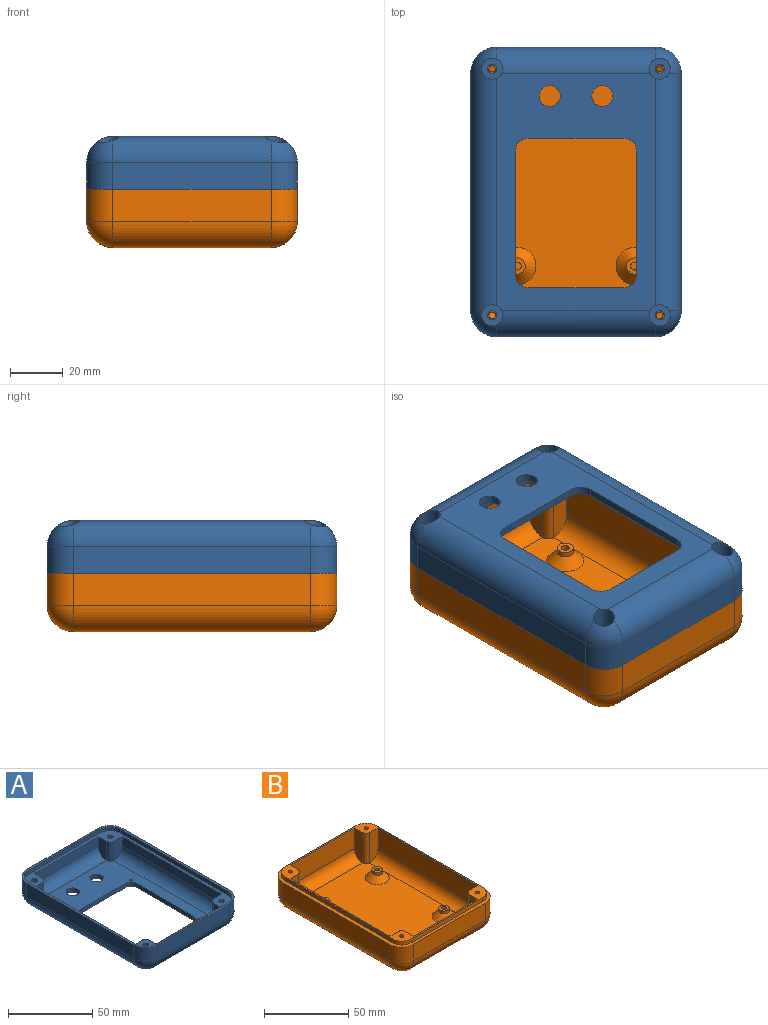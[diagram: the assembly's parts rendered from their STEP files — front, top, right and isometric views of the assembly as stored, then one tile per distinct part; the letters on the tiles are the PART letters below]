
ASSEMBLY  parts=2 mates=1
PART A: 78 faces, bbox 80x110x20 mm
  f0: plane 90x60mm, normal (0,0,-1), area 2700.5mm2, adj f1,f3,f4,f6,f31,f32,f33,f34
  f1: cylinder r=10mm len=90mm, axis (0,1,0), area 1394.3mm2, adj f0,f2,f11,f23,f65,f66
  f2: sphere r=10mm, area 123.8mm2, adj f1,f3,f30,f65
  f3: cylinder r=10mm len=60mm, axis (1,0,0), area 923.1mm2, adj f0,f2,f12,f29,f62,f65
  f4: cylinder r=10mm len=60mm, axis (-1,0,0), area 923.1mm2, adj f0,f5,f11,f25,f66,f69
  f5: sphere r=10mm, area 123.8mm2, adj f4,f6,f26,f69
  f6: cylinder r=10mm len=90mm, axis (0,-1,0), area 1394.3mm2, adj f0,f5,f12,f27,f62,f69
  f7: cylinder r=1.75mm len=3.5mm, axis (0,0,1), area 22mm2, adj f49,f68
  f8: cylinder r=1.75mm len=3.5mm, axis (0,0,1), area 22mm2, adj f49,f67
  f9: cylinder r=1.75mm len=3.5mm, axis (0,0,1), area 22mm2, adj f49,f64
  f10: cylinder r=1.75mm len=3.5mm, axis (0,0,1), area 22mm2, adj f49,f63
  f11: sphere r=10mm, area 123.8mm2, adj f1,f4,f24,f66
  f12: sphere r=10mm, area 123.8mm2, adj f3,f6,f28,f62
  f13: plane 84x7mm, normal (1,0,0), area 588mm2, adj f21,f49,f52,f61
  f14: plane 54x7mm, normal (0,1,0), area 378mm2, adj f18,f49,f56,f60
  f15: plane 84x7mm, normal (-1,0,0), area 588mm2, adj f17,f49,f55,f58
  f16: plane 90x60mm, normal (0,0,1), area 2667.3mm2, adj f17,f18,f20,f21,f31,f32,f33,f34
  f17: cylinder r=7mm len=84mm, axis (0,1,0), area 923.6mm2, adj f15,f16,f55,f58
  f18: cylinder r=7mm len=54mm, axis (1,0,0), area 593.8mm2, adj f14,f16,f56,f60
  f19: plane 54x7mm, normal (0,-1,0), area 378mm2, adj f20,f49,f50,f54
  f20: cylinder r=7mm len=54mm, axis (-1,0,0), area 593.8mm2, adj f16,f19,f50,f54
  f21: cylinder r=7mm len=84mm, axis (0,-1,0), area 923.6mm2, adj f13,f16,f52,f61
  f22: plane 110x80mm, normal (0,0,1), area 484.1mm2, adj f23,f24,f25,f26,f27,f28,f29,f30
  f23: plane 90x10mm, normal (1,0,0), area 900mm2, adj f1,f22,f24,f30
  f24: cylinder r=10mm len=10mm, axis (0,0,-1), area 157.1mm2, adj f11,f22,f23,f25
  f25: plane 60x10mm, normal (0,1,0), area 600mm2, adj f4,f22,f24,f26
  f26: cylinder r=10mm len=10mm, axis (0,0,-1), area 157.1mm2, adj f5,f22,f25,f27
  f27: plane 90x10mm, normal (-1,0,0), area 900mm2, adj f6,f22,f26,f28
  f28: cylinder r=10mm len=10mm, axis (0,0,-1), area 157.1mm2, adj f12,f22,f27,f29
  f29: plane 60x10mm, normal (0,-1,0), area 600mm2, adj f3,f22,f28,f30
  f30: cylinder r=10mm len=10mm, axis (0,0,-1), area 157.1mm2, adj f2,f22,f23,f29
  f31: cylinder r=4mm len=8mm, axis (0,0,1), area 75.4mm2, adj f0,f16
  f32: cylinder r=4mm len=8mm, axis (0,0,1), area 75.4mm2, adj f0,f16
  f33: plane 46.8x3mm, normal (-1,0,0), area 140.4mm2, adj f0,f16,f34,f40
  f34: cylinder r=5mm len=5mm, axis (0,0,1), area 23.6mm2, adj f0,f16,f33,f35
  f35: plane 36x3mm, normal (0,-1,0), area 108mm2, adj f0,f16,f34,f36
  f36: cylinder r=5mm len=5mm, axis (0,0,1), area 23.6mm2, adj f0,f16,f35,f37
  f37: plane 46.8x3mm, normal (1,0,0), area 140.4mm2, adj f0,f16,f36,f38
  f38: cylinder r=5mm len=5mm, axis (0,0,1), area 23.6mm2, adj f0,f16,f37,f39
  f39: plane 36x3mm, normal (0,1,0), area 108mm2, adj f0,f16,f38,f40
  f40: cylinder r=5mm len=5mm, axis (0,0,1), area 23.6mm2, adj f0,f16,f33,f39
  f41: plane 90x3mm, normal (1,0,0), area 270mm2, adj f22,f42,f48,f49
  f42: cylinder r=8.65mm len=8.65mm, axis (0,0,1), area 40.8mm2, adj f22,f41,f43,f49
  f43: plane 60x3mm, normal (0,1,0), area 180mm2, adj f22,f42,f44,f49
  f44: cylinder r=8.65mm len=8.65mm, axis (0,0,1), area 40.8mm2, adj f22,f43,f45,f49
  f45: plane 90x3mm, normal (-1,0,0), area 270mm2, adj f22,f44,f46,f49
  f46: cylinder r=8.65mm len=8.65mm, axis (0,0,1), area 40.8mm2, adj f22,f45,f47,f49
  f47: plane 60x3mm, normal (0,-1,0), area 180mm2, adj f22,f46,f48,f49
  f48: cylinder r=8.65mm len=8.65mm, axis (0,0,1), area 40.8mm2, adj f22,f41,f47,f49
  f49: plane 107.3x77.3mm, normal (0,0,1), area 887.9mm2, adj f7,f8,f9,f10,f13,f14,f15,f19
  f50: plane 14x7mm, normal (1,0,0), area 87.5mm2, adj f19,f20,f49,f51
  f51: cylinder r=3mm len=14mm, axis (0,0,1), area 66mm2, adj f16,f49,f50,f52
  f52: plane 14x7mm, normal (0,-1,0), area 87.5mm2, adj f13,f21,f49,f51
  f53: cylinder r=3mm len=14mm, axis (0,0,1), area 66mm2, adj f16,f49,f54,f55
  f54: plane 14x7mm, normal (-1,0,0), area 87.5mm2, adj f19,f20,f49,f53
  f55: plane 14x7mm, normal (0,-1,0), area 87.5mm2, adj f15,f17,f49,f53
  f56: plane 14x7mm, normal (-1,0,0), area 87.5mm2, adj f14,f18,f49,f57
  f57: cylinder r=3mm len=14mm, axis (0,0,1), area 66mm2, adj f16,f49,f56,f58
  f58: plane 14x7mm, normal (0,1,0), area 87.5mm2, adj f15,f17,f49,f57
  f59: cylinder r=3mm len=14mm, axis (0,0,1), area 66mm2, adj f16,f49,f60,f61
  f60: plane 14x7mm, normal (1,0,0), area 87.5mm2, adj f14,f18,f49,f59
  f61: plane 14x7mm, normal (0,1,0), area 87.5mm2, adj f13,f21,f49,f59
  f62: cylinder r=4mm len=15mm, axis (0,0,-1), area 348.3mm2, adj f0,f3,f6,f12,f63
  f63: plane 8x8mm, normal (0,0,-1), area 40.6mm2, adj f10,f62
  f64: plane 8x8mm, normal (0,0,-1), area 40.6mm2, adj f9,f65
  f65: cylinder r=4mm len=15mm, axis (0,0,-1), area 348.2mm2, adj f0,f1,f2,f3,f64
  f66: cylinder r=4mm len=15mm, axis (0,0,-1), area 348.2mm2, adj f0,f1,f4,f11,f67
  f67: plane 8x8mm, normal (0,0,-1), area 40.6mm2, adj f8,f66
  f68: plane 8x8mm, normal (0,0,-1), area 40.6mm2, adj f7,f69
  f69: cylinder r=4mm len=15mm, axis (0,0,-1), area 348.3mm2, adj f0,f4,f5,f6,f68
  f70: cylinder r=1mm len=2mm, axis (0,0,1), area 12.6mm2, adj f16,f71
  f71: plane 2x2mm, normal (0,0,1), area 3.1mm2, adj f70
  f72: cylinder r=1mm len=2mm, axis (0,0,1), area 12.6mm2, adj f16,f73
  f73: plane 2x2mm, normal (0,0,1), area 3.1mm2, adj f72
  f74: cylinder r=1mm len=2mm, axis (0,0,1), area 12.6mm2, adj f16,f75
  f75: plane 2x2mm, normal (0,0,1), area 3.1mm2, adj f74
  f76: cylinder r=1mm len=2mm, axis (0,0,1), area 12.6mm2, adj f16,f77
  f77: plane 2x2mm, normal (0,0,1), area 3.1mm2, adj f76
PART B: 76 faces, bbox 80x110x25 mm
  f0: plane 54x15mm, normal (0,1,0), area 810mm2, adj f4,f9,f48,f52
  f1: plane 84x15mm, normal (-1,0,0), area 1260mm2, adj f7,f9,f42,f54
  f2: plane 90x60mm, normal (0,0,1), area 4738.3mm2, adj f4,f5,f7,f8,f37,f43,f47,f53
  f3: plane 84x15mm, normal (1,0,0), area 1260mm2, adj f5,f9,f38,f46
  f4: cylinder r=7mm len=54mm, axis (1,0,0), area 593.8mm2, adj f0,f2,f48,f52
  f5: cylinder r=7mm len=84mm, axis (0,-1,0), area 923.6mm2, adj f2,f3,f38,f46
  f6: plane 54x15mm, normal (0,-1,0), area 810mm2, adj f8,f9,f39,f41
  f7: cylinder r=7mm len=84mm, axis (0,1,0), area 923.6mm2, adj f1,f2,f42,f54
  f8: cylinder r=7mm len=54mm, axis (-1,0,0), area 593.8mm2, adj f2,f6,f39,f41
  f9: plane 105.6x75.6mm, normal (0,0,1), area 607.8mm2, adj f0,f1,f3,f6,f10,f11,f12,f13
  f10: cylinder r=7.8mm len=7.8mm, axis (0,0,1), area 34.3mm2, adj f9,f11,f17,f18
  f11: plane 90x2.8mm, normal (-1,0,0), area 252mm2, adj f9,f10,f12,f18
  f12: cylinder r=7.8mm len=7.8mm, axis (0,0,1), area 34.3mm2, adj f9,f11,f13,f18
  f13: plane 60x2.8mm, normal (0,1,0), area 168mm2, adj f9,f12,f14,f18
  f14: cylinder r=7.8mm len=7.8mm, axis (0,0,1), area 34.3mm2, adj f9,f13,f15,f18
  f15: plane 90x2.8mm, normal (1,0,0), area 252mm2, adj f9,f14,f16,f18
  f16: cylinder r=7.8mm len=7.8mm, axis (0,0,1), area 34.3mm2, adj f9,f15,f17,f18
  f17: plane 60x2.8mm, normal (0,-1,0), area 168mm2, adj f9,f10,f16,f18
  f18: plane 110x80mm, normal (0,0,1), area 783mm2, adj f10,f11,f12,f13,f14,f15,f16,f17
  f19: plane 90x60mm, normal (0,0,-1), area 5400mm2, adj f20,f22,f24,f26
  f20: cylinder r=10mm len=90mm, axis (0,1,0), area 1413.7mm2, adj f19,f21,f27,f35
  f21: sphere r=10mm, area 157.1mm2, adj f20,f22,f34
  f22: cylinder r=10mm len=60mm, axis (-1,0,0), area 942.5mm2, adj f19,f21,f23,f33
  f23: sphere r=10mm, area 157.1mm2, adj f22,f24,f32
  f24: cylinder r=10mm len=90mm, axis (0,-1,0), area 1413.7mm2, adj f19,f23,f25,f31
  f25: sphere r=10mm, area 157.1mm2, adj f24,f26,f30
  f26: cylinder r=10mm len=60mm, axis (1,0,0), area 942.5mm2, adj f19,f25,f27,f29
  f27: sphere r=10mm, area 157.1mm2, adj f20,f26,f28
  f28: cylinder r=10mm len=12.2mm, axis (0,0,-1), area 191.6mm2, adj f18,f27,f29,f35
  f29: plane 60x12.2mm, normal (0,-1,0), area 732mm2, adj f18,f26,f28,f30
  f30: cylinder r=10mm len=12.2mm, axis (0,0,-1), area 191.6mm2, adj f18,f25,f29,f31
  f31: plane 90x12.2mm, normal (-1,0,0), area 1098mm2, adj f18,f24,f30,f32
  f32: cylinder r=10mm len=12.2mm, axis (0,0,-1), area 191.6mm2, adj f18,f23,f31,f33
  f33: plane 60x12.2mm, normal (0,1,0), area 732mm2, adj f18,f22,f32,f34
  f34: cylinder r=10mm len=12.2mm, axis (0,0,-1), area 191.6mm2, adj f18,f21,f33,f35
  f35: plane 90x12.2mm, normal (1,0,0), area 1098mm2, adj f18,f20,f28,f34
  f36: cylinder r=1.25mm len=21.88mm, axis (0,0,1), area 168mm2, adj f9,f40
  f37: cylinder r=3mm len=22mm, axis (0,0,1), area 103.7mm2, adj f2,f9,f38,f39
  f38: plane 22x7mm, normal (0,-1,0), area 143.5mm2, adj f3,f5,f9,f37
  f39: plane 22x7mm, normal (1,0,0), area 143.5mm2, adj f6,f8,f9,f37
  f40: sphere r=7mm, area 5.3mm2, adj f36
  f41: plane 22x7mm, normal (-1,0,0), area 143.5mm2, adj f6,f8,f9,f43
  f42: plane 22x7mm, normal (0,-1,0), area 143.5mm2, adj f1,f7,f9,f43
  f43: cylinder r=3mm len=22mm, axis (0,0,1), area 103.7mm2, adj f2,f9,f41,f42
  f44: cylinder r=1.25mm len=21.88mm, axis (0,0,1), area 168mm2, adj f9,f45
  f45: sphere r=7mm, area 5.3mm2, adj f44
  f46: plane 22x7mm, normal (0,1,0), area 143.5mm2, adj f3,f5,f9,f47
  f47: cylinder r=3mm len=22mm, axis (0,0,1), area 103.7mm2, adj f2,f9,f46,f48
  f48: plane 22x7mm, normal (1,0,0), area 143.5mm2, adj f0,f4,f9,f47
  f49: cylinder r=1.25mm len=21.88mm, axis (0,0,1), area 168mm2, adj f9,f50
  f50: sphere r=7mm, area 5.3mm2, adj f49
  f51: cylinder r=1.25mm len=21.88mm, axis (0,0,1), area 168mm2, adj f9,f55
  f52: plane 22x7mm, normal (-1,0,0), area 143.5mm2, adj f0,f4,f9,f53
  f53: cylinder r=3mm len=22mm, axis (0,0,1), area 103.7mm2, adj f2,f9,f52,f54
  f54: plane 22x7mm, normal (0,1,0), area 143.5mm2, adj f1,f7,f9,f53
  f55: sphere r=7mm, area 5.3mm2, adj f51
  f56: cylinder r=1.5mm len=6mm, axis (0,0,1), area 56.5mm2, adj f58,f59
  f57: cylinder r=3.1mm len=6.2mm, axis (0,0,1), area 39mm2, adj f58,f75
  f58: plane 6.2x6.2mm, normal (0,0,1), area 23.1mm2, adj f56,f57
  f59: plane 3x3mm, normal (0,0,1), area 7.1mm2, adj f56
  f60: cylinder r=1.5mm len=6mm, axis (0,0,1), area 56.5mm2, adj f62,f63
  f61: cylinder r=3.1mm len=6.2mm, axis (0,0,1), area 39mm2, adj f62,f74
  f62: plane 6.2x6.2mm, normal (0,0,1), area 23.1mm2, adj f60,f61
  f63: plane 3x3mm, normal (0,0,1), area 7.1mm2, adj f60
  f64: cylinder r=1.5mm len=6mm, axis (0,0,1), area 56.5mm2, adj f66,f67
  f65: cylinder r=3.1mm len=6.2mm, axis (0,0,1), area 39mm2, adj f66,f73
  f66: plane 6.2x6.2mm, normal (0,0,1), area 23.1mm2, adj f64,f65
  f67: plane 3x3mm, normal (0,0,1), area 7.1mm2, adj f64
  f68: cylinder r=1.5mm len=6mm, axis (0,0,1), area 56.5mm2, adj f70,f71
  f69: cylinder r=3.1mm len=6.2mm, axis (0,0,1), area 39mm2, adj f70,f72
  f70: plane 6.2x6.2mm, normal (0,0,1), area 23.1mm2, adj f68,f69
  f71: plane 3x3mm, normal (0,0,1), area 7.1mm2, adj f68
  f72: cone r=3.1mm half-angle=45deg, axis (0,0,-1), area 181.3mm2, adj f2,f69
  f73: cone r=3.1mm half-angle=45deg, axis (0,0,-1), area 181.3mm2, adj f2,f65
  f74: cone r=3.1mm half-angle=45deg, axis (0,0,-1), area 181.3mm2, adj f2,f61
  f75: cone r=3.1mm half-angle=45deg, axis (0,0,-1), area 181.3mm2, adj f2,f57
PLACE A rot(axis=(0,1,0),180deg) t=(50.3,-18.33,63.68)mm
PLACE B t=(50.3,-18.33,21.48)mm
MATE fastened B.f14 <-> A.f26  axis (0,0,1) through (80.3,26.67,43.68)mm
